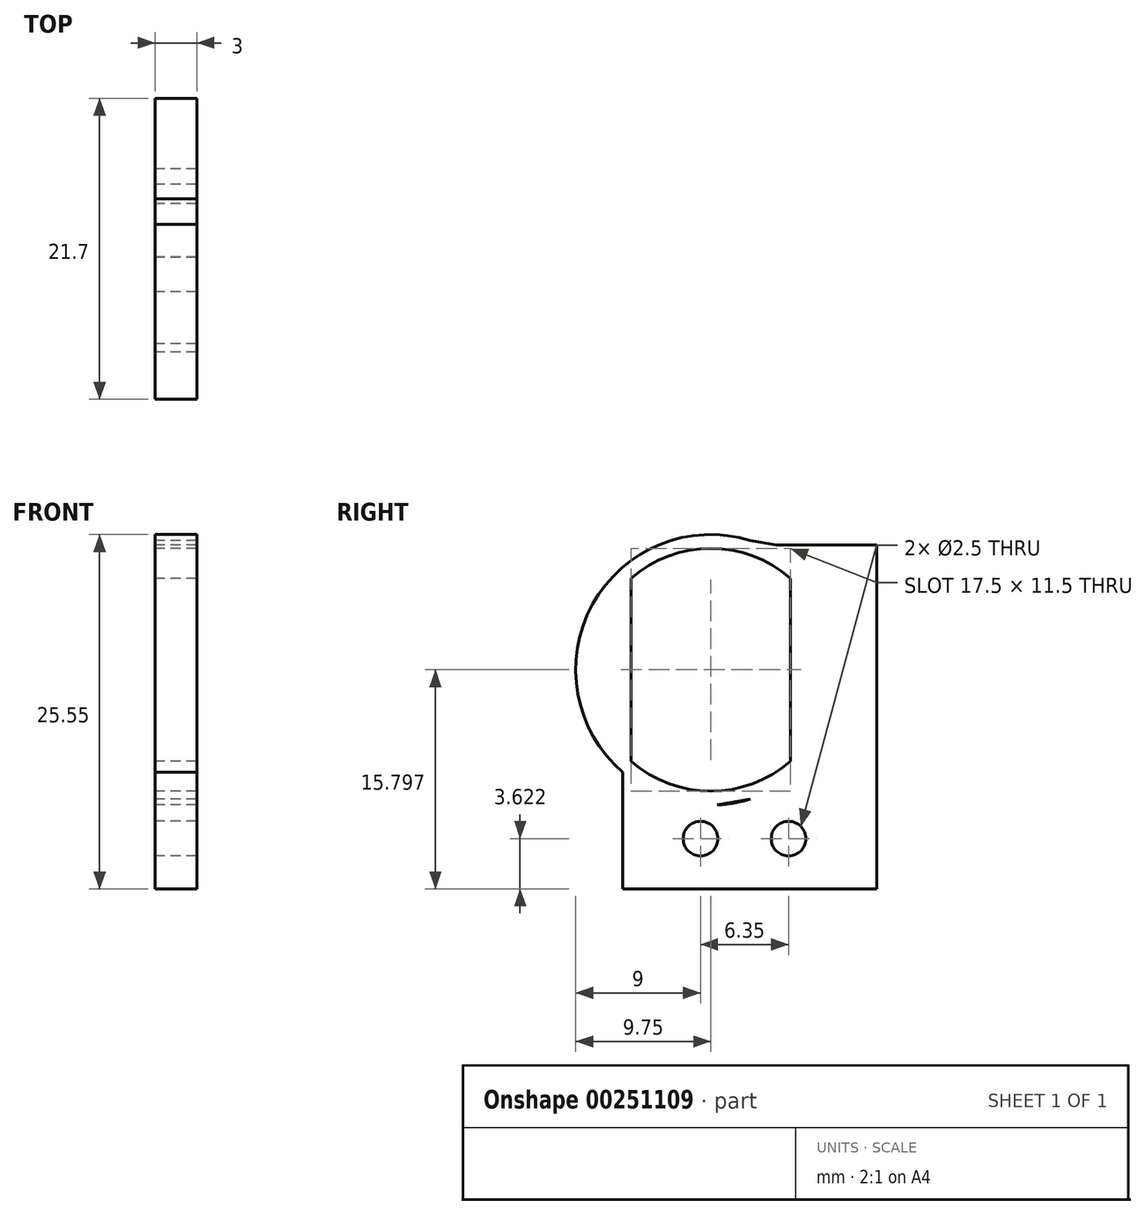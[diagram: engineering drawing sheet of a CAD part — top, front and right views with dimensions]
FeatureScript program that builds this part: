
annotation { "Feature Type Name" : "Feature", "Feature Type Description" : "" }
export const myFeature = defineFeature(function(context is Context, id is Id, definition is map)
    precondition{}
    {
        {
            var Q0;
            Q0=qCreatedBy(makeId("Right.planeOp"),FACE);
            var sketch = newSketch(context, id + "F0", { "sketchPlane" : qUnion([Q0])});
            skLineSegment(sketch, "E0", {"start": v(-11.95, -13.7) * mm, "end": v(-11.95, -5.31) * mm});
            skCircle(sketch, "E1", {"center": v(-5.6, 2.09) * mm, "radius": 9.75 * mm});
            skCircle(sketch, "E2", {"center": v(-5.6, 2.09) * mm, "radius": 8.75 * mm});
            skLineSegment(sketch, "E3", {"start": v(-5.6, 2.09) * mm, "end": v(6.35, 2.09) * mm, "construction": true});
            skLineSegment(sketch, "E4", {"start": v(-0.03, 10.09) * mm, "end": v(5.35, 10.09) * mm});
            skLineSegment(sketch, "E5", {"start": v(5.35, 10.09) * mm, "end": v(5.35, 2.09) * mm});
            skLineSegment(sketch, "E6.MirrorCS", {"start": v(5.35, -5.91) * mm, "end": v(5.35, 2.09) * mm});
            skLineSegment(sketch, "E7.MirrorCS", {"start": v(-0.03, -5.91) * mm, "end": v(5.35, -5.91) * mm});
            skLineSegment(sketch, "E8.0", {"start": v(-0.9, -6.91) * mm, "end": v(6.35, -6.91) * mm});
            skLineSegment(sketch, "E8.1", {"start": v(6.35, -6.91) * mm, "end": v(6.35, 2.09) * mm});
            skLineSegment(sketch, "E8.2", {"start": v(6.35, 11.09) * mm, "end": v(6.35, 2.09) * mm});
            skLineSegment(sketch, "E8.3", {"start": v(-0.9, 11.09) * mm, "end": v(6.35, 11.09) * mm});
            skLineSegment(sketch, "E9", {"start": v(-0.9, 11.09) * mm, "end": v(-5.13, 11.83) * mm});
            skLineSegment(sketch, "E10.MirrorCS", {"start": v(-0.9, -6.91) * mm, "end": v(-5.13, -7.65) * mm});
            skLineSegment(sketch, "E11", {"start": v(5.35, 8.12) * mm, "end": v(6.35, 8.12) * mm});
            skLineSegment(sketch, "E12.MirrorCS", {"start": v(5.35, -3.95) * mm, "end": v(6.35, -3.95) * mm});
            skLineSegment(sketch, "E13", {"start": v(-0.03, 10.09) * mm, "end": v(-2.99, 10.44) * mm});
            skLineSegment(sketch, "E14.MirrorCS", {"start": v(-0.03, -5.91) * mm, "end": v(-2.99, -6.26) * mm});
            skLineSegment(sketch, "E15", {"start": v(6.35, -6.91) * mm, "end": v(6.35, -13.7) * mm});
            skLineSegment(sketch, "E16", {"start": v(-11.95, -13.7) * mm, "end": v(6.35, -13.7) * mm});
            skCircle(sketch, "E17", {"center": v(-6.35, -10.09) * mm, "radius": 1.25 * mm});
            skCircle(sketch, "E18", {"center": v(0, -10.09) * mm, "radius": 1.25 * mm});
            skLineSegment(sketch, "E19", {"start": v(-11.35, -4.5) * mm, "end": v(-11.35, 8.68) * mm});
            skLineSegment(sketch, "E20", {"start": v(-5.6, 10.84) * mm, "end": v(-5.6, -6.66) * mm, "construction": true});
            skLineSegment(sketch, "E21.MirrorCS", {"start": v(0.15, -4.5) * mm, "end": v(0.15, 8.68) * mm});
            skSolve(sketch);
        }
        {
            var Q0;
            Q0=qSketchRegion(id+"F0",true);
            var Q1;
            {var subQ0=sQuery(id+"F0.wireOp",EDGE,"E13");Q1=makeQuery(id+"F0.imprint","IMPRINT",FACE,{"disambiguationData":[TD([[makeQuery(id+"F0.imprint","IMPRINT",EDGE,{"derivedFrom":subQ0}),1.0]])]});}
            var Q2;
            {var subQ4=sQuery(id+"F0.wireOp",EDGE,"E4");Q2=makeQuery(id+"F0.imprint","IMPRINT",FACE,{"disambiguationData":[TD([[makeQuery(id+"F0.imprint","IMPRINT",EDGE,{"derivedFrom":subQ4}),-1.0]])]});}
            var Q3;
            {var subQ0=sQuery(id+"F0.wireOp",EDGE,"E19");Q3=makeQuery(id+"F0.imprint","IMPRINT",FACE,{"disambiguationData":[TD([[makeQuery(id+"F0.imprint","IMPRINT",EDGE,{"derivedFrom":subQ0}),1.0]])]});}
            var Q4;
            {var subQ0=sQuery(id+"F0.wireOp",EDGE,"E21.MirrorCS");Q4=makeQuery(id+"F0.imprint","IMPRINT",FACE,{"disambiguationData":[TD([[makeQuery(id+"F0.imprint","IMPRINT",EDGE,{"derivedFrom":subQ0}),-1.0]])]});}
            var Q5;
            {var subQ0=sQuery(id+"F0.wireOp",EDGE,"E10.MirrorCS");var subQ1=sQuery(id+"F0.wireOp",EDGE,"E1");var subQ2=makeQuery(id+"F0.imprint","INTERSECT",VERTEX,{"disambiguationData":[OD(0.0)],"derivedFrom":[subQ1,subQ0]});Q5=makeQuery(id+"F0.imprint","IMPRINT",FACE,{"disambiguationData":[TD([[makeQuery(id+"F0.imprint","IMPRINT",EDGE,{"disambiguationData":[TD([[subQ2,-1.0]])],"derivedFrom":subQ1}),1.0]])]});}
            extrude(context, id + "F1", {"entities" : qUnion([Q0, Q1, Q2, Q3, Q4, Q5]), "depth" : 3 * mm});
        }
    });
